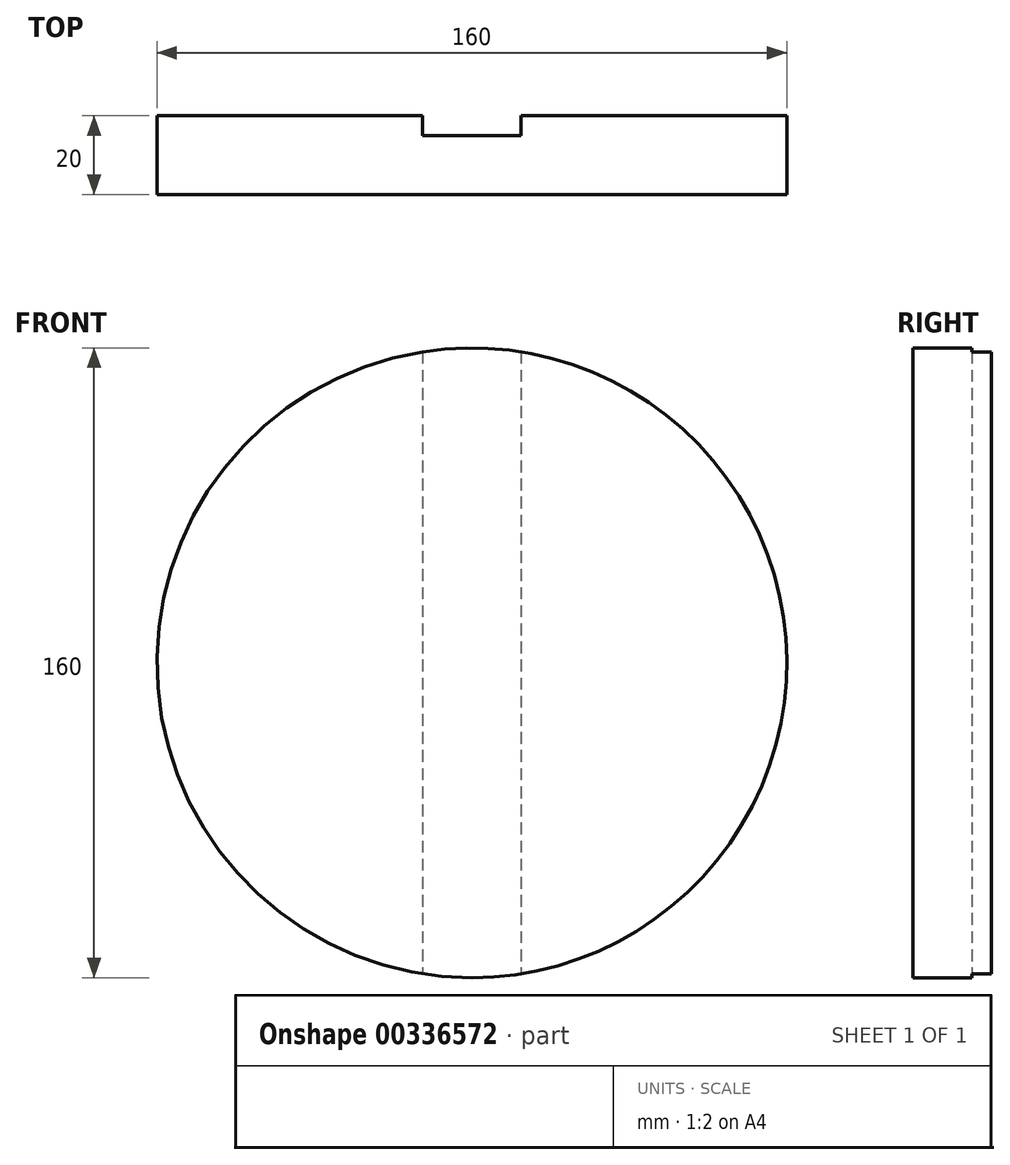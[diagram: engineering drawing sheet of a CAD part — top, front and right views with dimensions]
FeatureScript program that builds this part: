
annotation { "Feature Type Name" : "Feature", "Feature Type Description" : "" }
export const myFeature = defineFeature(function(context is Context, id is Id, definition is map)
    precondition{}
    {
        {
            var Q0;
            Q0=qCreatedBy(makeId("Front.planeOp"),FACE);
            var sketch = newSketch(context, id + "F0", { "sketchPlane" : qUnion([Q0])});
            skCircle(sketch, "E0", {"center": v(0, 0) * mm, "radius": 80 * mm});
            skSolve(sketch);
        }
        {
            var Q0;
            Q0 = qSketchRegion(id + "F0", true);
            extrude(context, id + "F1", {"entities" : qUnion([Q0]), "depth" : 20 * mm, "offsetDistance" : 25 * mm});
        }
        {
            var Q0;
            Q0=qCreatedBy(makeId("Front.planeOp"),FACE);
            var sketch = newSketch(context, id + "F2", { "sketchPlane" : qUnion([Q0])});
            skLineSegment(sketch, "E1.bottom", {"start": v(-12.5, 80) * mm, "end": v(12.5, 80) * mm});
            skLineSegment(sketch, "E1.top", {"start": v(-12.5, -80) * mm, "end": v(12.5, -80) * mm});
            skLineSegment(sketch, "E1.left", {"start": v(-12.5, 80) * mm, "end": v(-12.5, -80) * mm});
            skLineSegment(sketch, "E1.right", {"start": v(12.5, 80) * mm, "end": v(12.5, -80) * mm});
            skPoint(sketch, "E1.middle", {"position": v(0, 0) * mm});
            skSolve(sketch);
        }
        {
            var Q0;
            Q0 = qSketchRegion(id + "F2", true);
            extrude(context, id + "F3", {"entities" : qUnion([Q0]), "operationType" : NewBodyOperationType.REMOVE, "depth" : 5 * mm, "offsetDistance" : 25 * mm});
        }
    });
